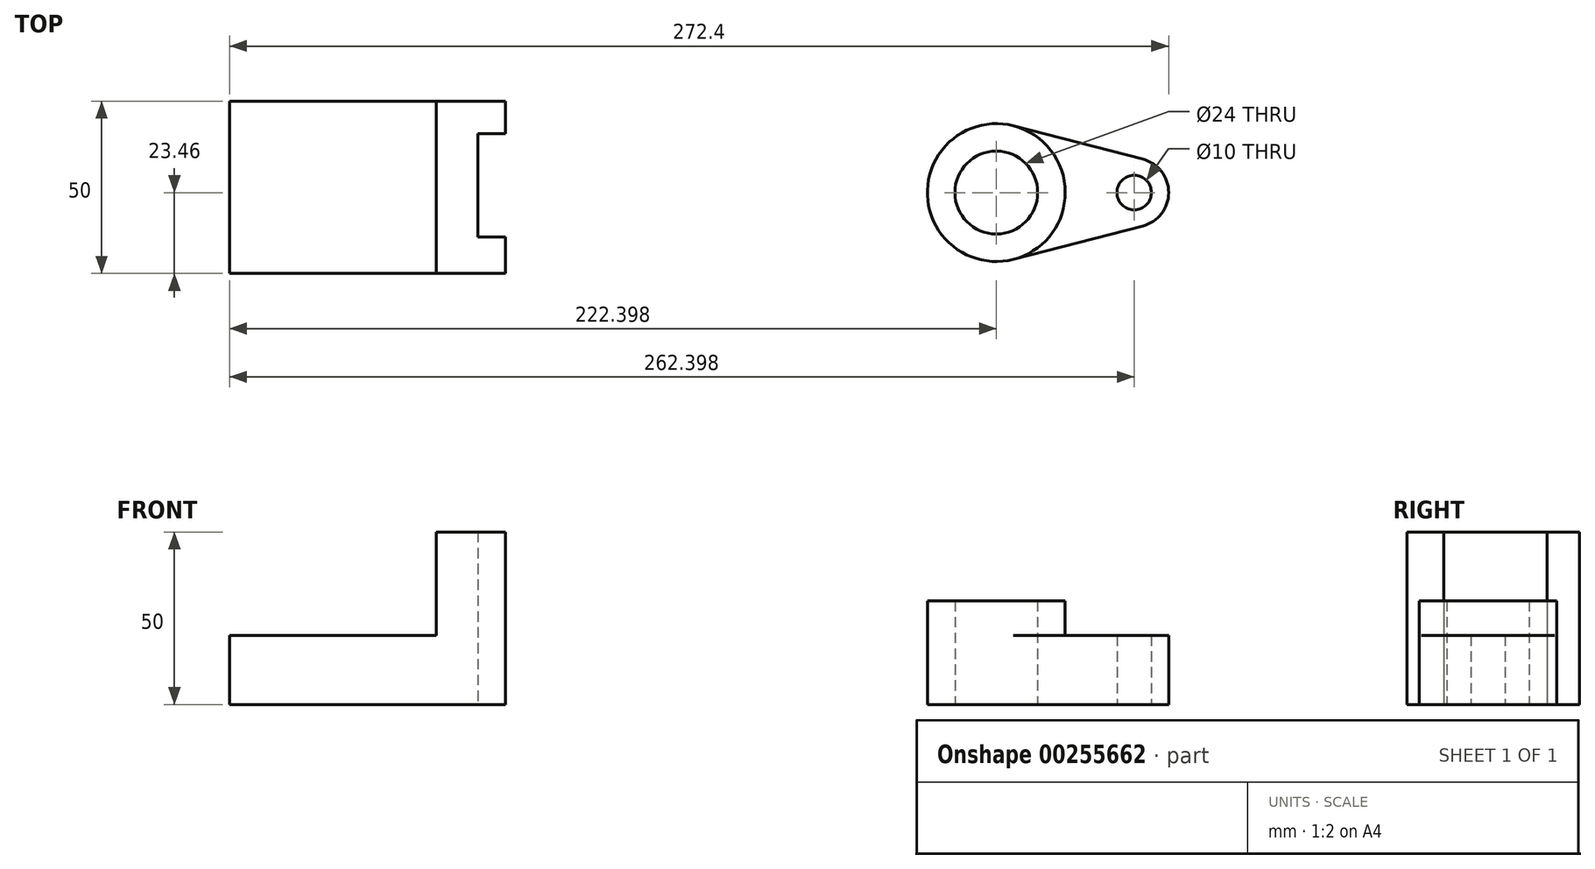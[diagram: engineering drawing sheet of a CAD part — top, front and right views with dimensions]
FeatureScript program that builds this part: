
annotation { "Feature Type Name" : "Feature", "Feature Type Description" : "" }
export const myFeature = defineFeature(function(context is Context, id is Id, definition is map)
    precondition{}
    {
        {
            var Q0;
            Q0=qCreatedBy(makeId("Top.planeOp"),FACE);
            var sketch = newSketch(context, id + "F0", { "sketchPlane" : qUnion([Q0])});
            skLineSegment(sketch, "E0.bottom", {"start": v(-25.9, 26.54) * mm, "end": v(34.1, 26.54) * mm});
            skLineSegment(sketch, "E0.top", {"start": v(-25.9, -23.46) * mm, "end": v(34.1, -23.46) * mm});
            skLineSegment(sketch, "E0.left", {"start": v(-25.9, 26.54) * mm, "end": v(-25.9, -23.46) * mm});
            skLineSegment(sketch, "E0.right", {"start": v(34.1, 26.54) * mm, "end": v(34.1, -23.46) * mm});
            skLineSegment(sketch, "E1.bottom", {"start": v(34.1, 26.54) * mm, "end": v(54.1, 26.54) * mm});
            skLineSegment(sketch, "E1.top", {"start": v(34.1, -23.46) * mm, "end": v(54.1, -23.46) * mm});
            skLineSegment(sketch, "E1.right", {"start": v(54.1, 26.54) * mm, "end": v(54.1, 17.11) * mm});
            skLineSegment(sketch, "E2", {"start": v(54.1, 17.11) * mm, "end": v(46.1, 17.11) * mm});
            skLineSegment(sketch, "E3", {"start": v(46.1, 17.11) * mm, "end": v(46.1, -12.89) * mm});
            skLineSegment(sketch, "E4", {"start": v(46.1, -12.89) * mm, "end": v(54.1, -12.89) * mm});
            skLineSegment(sketch, "E5.trimOffspring", {"start": v(54.1, -12.89) * mm, "end": v(54.1, -23.46) * mm});
            skSolve(sketch);
        }
        {
            var Q0;
            Q0=makeQuery(id+"F0.imprint","IMPRINT",FACE,{"disambiguationData":[TD([[makeQuery(id+"F0.imprint","IMPRINT",EDGE,{"derivedFrom":sQuery(id+"F0.wireOp",EDGE,"E0.bottom")}),-1.0]])]});
            extrude(context, id + "F1", {"entities" : qUnion([Q0]), "depth" : 20 * mm});
        }
        {
            var Q0;
            Q0=makeQuery(id+"F0.imprint","IMPRINT",FACE,{"disambiguationData":[TD([[makeQuery(id+"F0.imprint","IMPRINT",EDGE,{"derivedFrom":sQuery(id+"F0.wireOp",EDGE,"E1.bottom")}),-1.0]])]});
            extrude(context, id + "F2", {"entities" : qUnion([Q0]), "operationType" : NewBodyOperationType.ADD, "depth" : 50 * mm});
        }
        {
            var Q0;
            Q0=qCreatedBy(makeId("Top.planeOp"),FACE);
            var sketch = newSketch(context, id + "F3", { "sketchPlane" : qUnion([Q0])});
            skCircle(sketch, "E6", {"center": v(196.5, 0) * mm, "radius": 20 * mm});
            skCircle(sketch, "E7", {"center": v(196.5, 0) * mm, "radius": 12 * mm});
            skCircle(sketch, "E8", {"center": v(236.5, 0) * mm, "radius": 5 * mm});
            skArc(sketch, "E9", {"start": v(239, -9.68) * mm, "mid": v(246.5, 0) * mm, "end": v(239, 9.68) * mm});
            skLineSegment(sketch, "E10", {"start": v(201.5, 19.36) * mm, "end": v(239, 9.68) * mm});
            skLineSegment(sketch, "E11", {"start": v(201.5, -19.36) * mm, "end": v(239, -9.68) * mm});
            skSolve(sketch);
        }
        {
            var Q0;
            Q0=makeQuery(id+"F3.imprint","IMPRINT",FACE,{"disambiguationData":[TD([[makeQuery(id+"F3.imprint","IMPRINT",EDGE,{"derivedFrom":sQuery(id+"F3.wireOp",EDGE,"E7")}),-1.0]])]});
            extrude(context, id + "F4", {"entities" : qUnion([Q0]), "depth" : 30 * mm});
        }
        {
            var Q0;
            Q0 = qSketchRegion(id + "F3", true);
            extrude(context, id + "F5", {"entities" : qUnion([Q0]), "operationType" : NewBodyOperationType.ADD, "depth" : 20 * mm});
        }
    });
